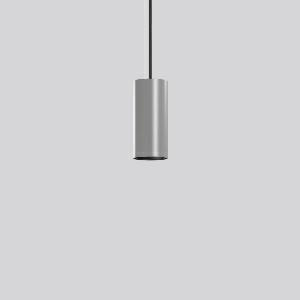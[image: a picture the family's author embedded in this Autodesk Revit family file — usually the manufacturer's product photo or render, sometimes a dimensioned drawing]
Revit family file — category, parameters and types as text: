
# Revit family: deecos_p_mini_911521_004_2_6274
name_source: partatom
category: Lighting Fixtures
units: mm (PartAtom-declared; Revit-internal decimal feet)

## family parameters
Cut with Voids When Loaded = No
Host = Face
Light Source = No
Part Type = Normal
Room Calculation Point = No
Round Connector Dimension = Use Diameter
Shared = No

## types (1)
- DEECOS P mini (1 x LED Modul 927, 3400 lm, 2700)
    Apparent Load = 29 VA
    Approval mark = CE
    CIE Flux Codes = 100 100 100 100 100
    Color Rendering = 92
    Color Temperature = 2700
    Default Elevation = 1800 mm
    Description = Series: DEECOS P mini
Cylindrical pendant luminaire. Housing: die-cast aluminium, powder-coated. Canopy made of powder-coated sheet steel with magnetic attachment. Optical assembly with reflector made of MIRO-Silver with 98% total light reflection for outstanding efficiency - can be changed without tools. Best colour rendering index Ra>90. Transparent pendant cable 5 m, can be shortened, with integrated steel cable. High quality converter without flickering and stroboscopic effect. The following accessories can be mounted without use of tools: interchangeable lenses, honeycomb louvre, clear and frosted diffusers, white interchangeable plastic ring. Decorative recessed suspension set available as accessory.Suitable for accessory Deecos P Tube cylinder extensions 0.5 m, 0.75 m or 1 m. 
Colour: silver
Diameter: 87 mm
Height: 195 mm
Suspension length: 5000 mm
Lamp: LED
Socket: without socket
Colour temperature: 2700K
Colour rendering index (CRI): 92
System power: 29 W
Rated luminous flux: 3400 lm
Luminous efficiency: 117 lm/W
Control gear: Regulated power supply
Protection class: I
Type of protection: IP 20
    Height = 195 mm
    Lamp = 1 x LED Modul 927
    Lamp Light Flux = 3400 lm
    Lamp count = 1
    Length = 87 mm
    Lifetime = 50000 h
    Luminous efficacy = 117 lm/W
    Manufacturer = RZB
    ModVariant = No
    Model = 911521.004.2
    Mounting Place = Ceiling
    Mounting Type = Pendant
    Number of Poles = 1
    OnlyDefault = Yes
    Power Factor = 1
    Product Name = DEECOS P mini
    Product group = Pendant luminaires
    ProductGroupID = 902
    Protection Class = Protection class I
    Protection Degree = IP 20
    RLX_Detail_Level = 1
    RLX_Emergency_Light_Flux = 0 lm
    RLX_Emergency_Type = 0
    RLX_Emergency_Type_DB = No
    RlxData = <blob elided: 55317 chars, md5=2aa6f361>
    Socket = socket
    Standby Power = 0 W
    System Light Flux = 3400 lm
    System Power = 29 W
    Type Comments = Product without accessories
    Type Image = 911476.004.jpg
    URL = http://relux.com
    VarID = ---
    Voltage = 230 V
    Voltage Range = 220-240 V
    Weight = 0.00 kg
    Width = 0 mm  [stored 0 ft]

note: [stored X ft] marks values corroborated as IEEE doubles in the binary element streams (Revit-internal decimal feet)

## geometry (parser evidence)
native form markers: Blend x4, Sweep x13
no freeform markers — native parametric forms only
